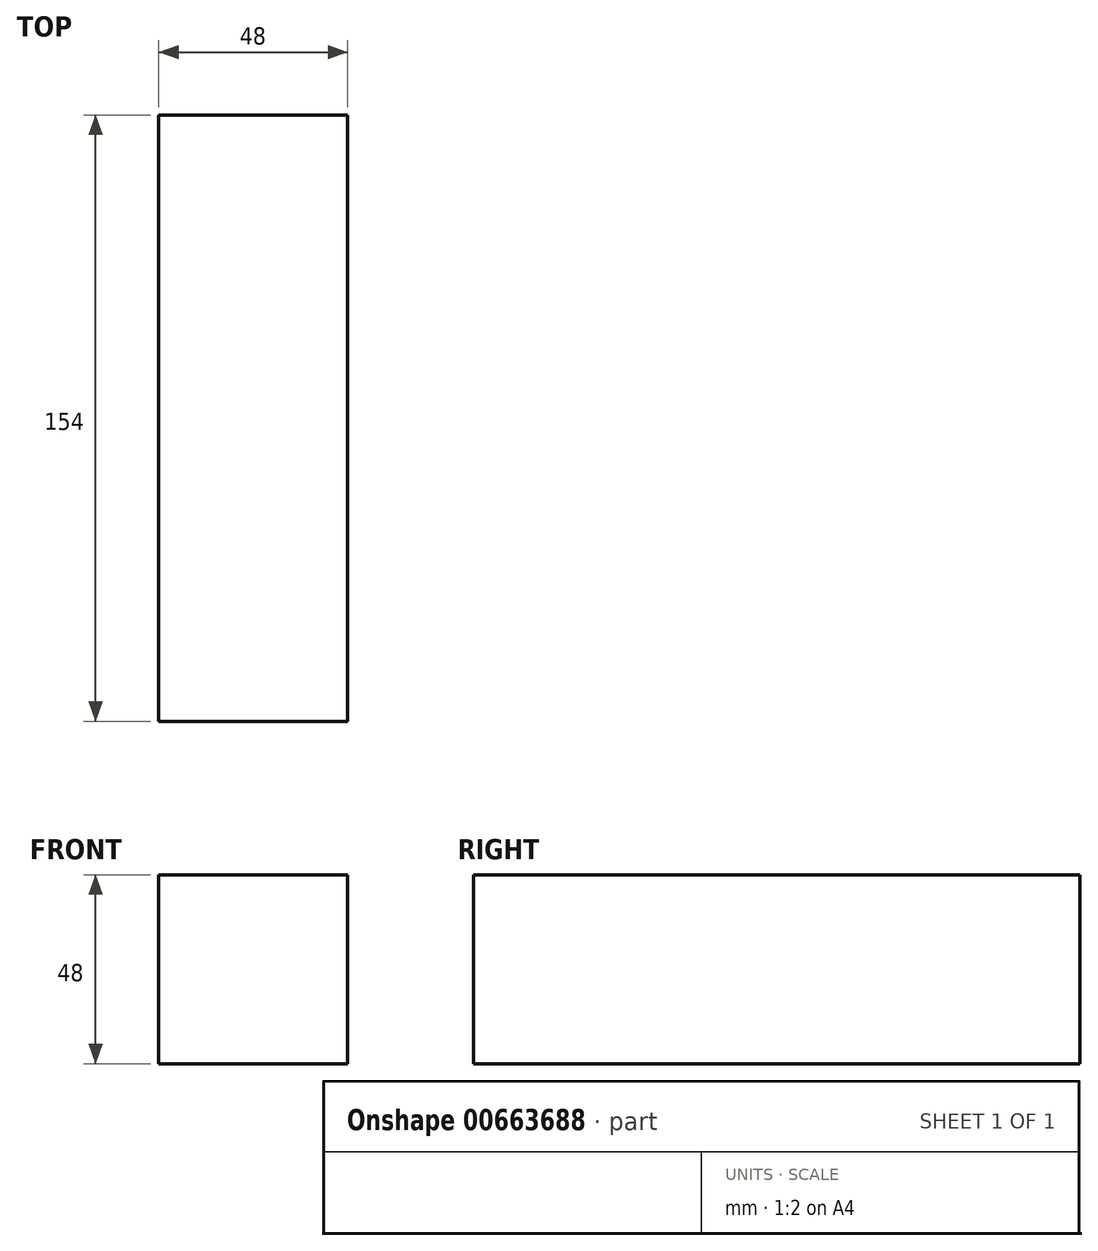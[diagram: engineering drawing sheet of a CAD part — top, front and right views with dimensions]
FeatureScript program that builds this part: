
annotation { "Feature Type Name" : "Feature", "Feature Type Description" : "" }
export const myFeature = defineFeature(function(context is Context, id is Id, definition is map)
    precondition{}
    {
        {
            var Q0;
            Q0=qCreatedBy(makeId("Front.planeOp"),FACE);
            var sketch = newSketch(context, id + "F0", { "sketchPlane" : qUnion([Q0])});
            skLineSegment(sketch, "E0.bottom", {"start": v(0, 0) * mm, "end": v(48, 0) * mm});
            skLineSegment(sketch, "E0.top", {"start": v(0, 48) * mm, "end": v(48, 48) * mm});
            skLineSegment(sketch, "E0.left", {"start": v(0, 0) * mm, "end": v(0, 48) * mm});
            skLineSegment(sketch, "E0.right", {"start": v(48, 0) * mm, "end": v(48, 48) * mm});
            skSolve(sketch);
        }
        {
            var Q0;
            Q0 = qSketchRegion(id + "F0", true);
            extrude(context, id + "F1", {"entities" : qUnion([Q0]), "depth" : 154 * mm, "offsetDistance" : 25 * mm});
        }
    });
